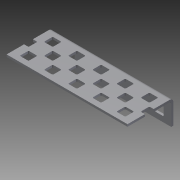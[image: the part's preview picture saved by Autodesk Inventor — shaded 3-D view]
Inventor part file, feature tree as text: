
AUTODESK INVENTOR PART (.ipt)
format: ipt  version: 2012 (Build 160160000, 160)  size: 826,880 bytes
history: native  units: in
note: dims shown in document units (in); Inventor stores cm internally (conversion verified against a paired STEP export)
features: plane x2, split x2, other x1, imported_body x1, extrude x1, sketch x1
ambient origin geometry x8: Origin, YZ Plane, XZ Plane, XY Plane, X Axis, Y Axis, Z Axis, Center Point
feature tree (8):
  parser-record x1  (decoder bookkeeping rows leaked as tree rows — omitted from the tree; the rows remain in map.json)
  imported_body  "Base1"
  plane  "Work Plane1"
  split  "Split1"
  plane  "Work Plane2"
  split  "Split2"
  extrude  "Extrusion1"  [1 undecoded]
  sketch  "Sketch1"  dims[d0=-1.0in d1=-9.0in d2=1.0in d3=0.0in]
note: 1 required parameter value undecoded (feature->parameter linkage not recoverable at this tier; creation-order binding heuristic only, values carry confidence <= 0.55)
